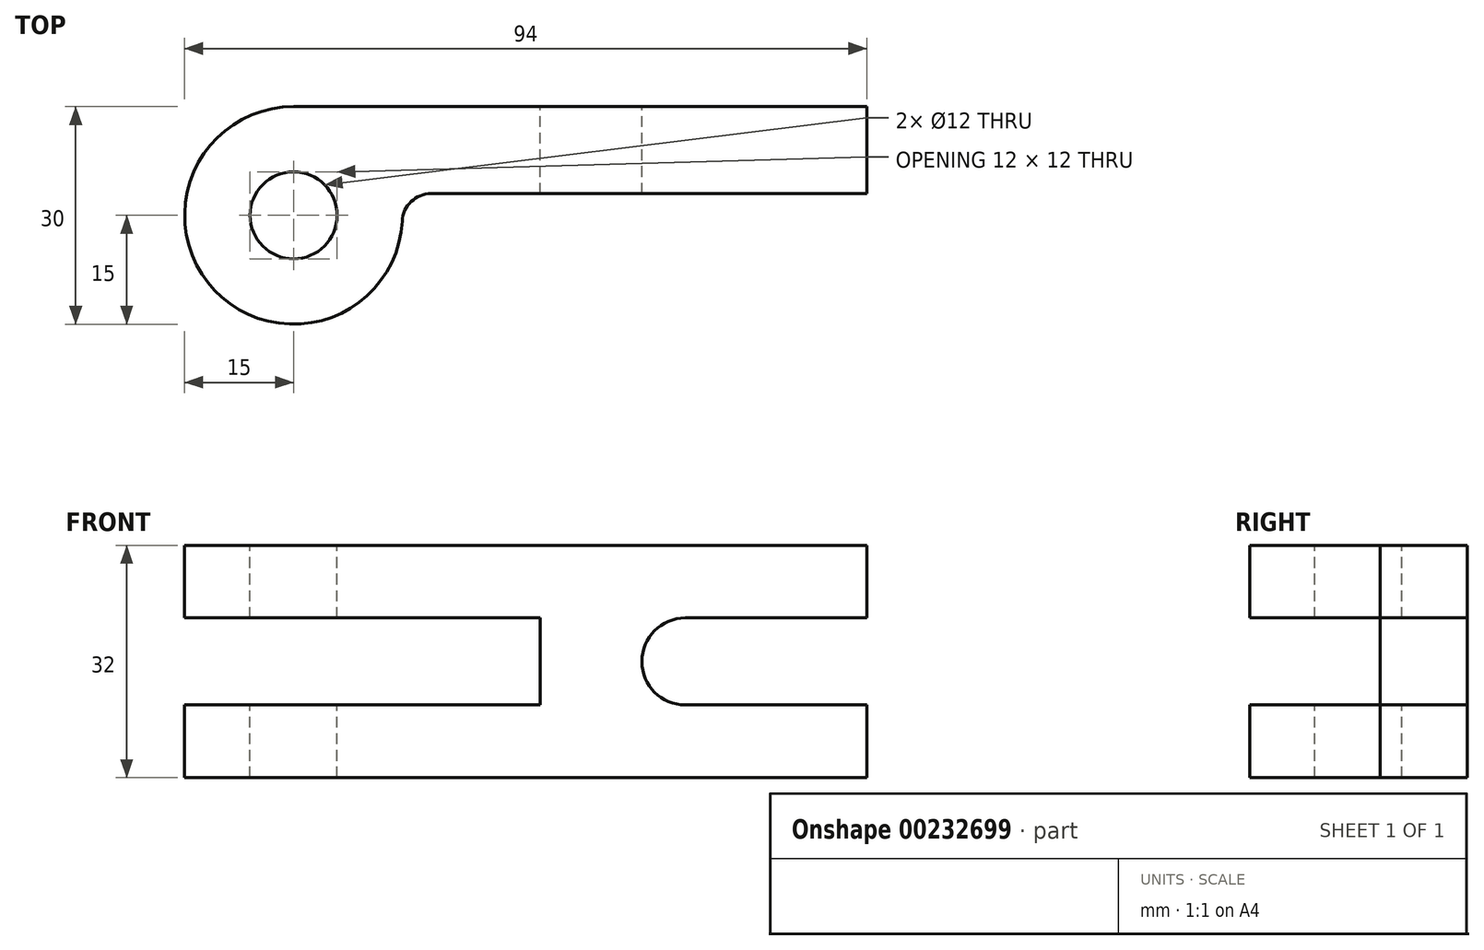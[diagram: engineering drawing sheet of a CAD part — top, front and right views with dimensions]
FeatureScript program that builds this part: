
annotation { "Feature Type Name" : "Feature", "Feature Type Description" : "" }
export const myFeature = defineFeature(function(context is Context, id is Id, definition is map)
    precondition{}
    {
        {
            var Q0;
            Q0=qCreatedBy(makeId("Front.planeOp"),FACE);
            var sketch = newSketch(context, id + "F0", { "sketchPlane" : qUnion([Q0])});
            skArc(sketch, "E0", {"start": v(0, -16) * mm, "mid": v(16, 0) * mm, "end": v(0, 16) * mm});
            skArc(sketch, "E1", {"start": v(0, -6) * mm, "mid": v(6, 0) * mm, "end": v(0, 6) * mm});
            skLineSegment(sketch, "E2", {"start": v(0, 16) * mm, "end": v(-94, 16) * mm});
            skLineSegment(sketch, "E3", {"start": v(-94, 16) * mm, "end": v(-94, 6) * mm});
            skLineSegment(sketch, "E4", {"start": v(-94, -16) * mm, "end": v(0, -16) * mm});
            skLineSegment(sketch, "E5", {"start": v(0, 6) * mm, "end": v(-25, 6) * mm});
            skLineSegment(sketch, "E6", {"start": v(0, -6) * mm, "end": v(-25, -6) * mm});
            skArc(sketch, "E7", {"start": v(-25, 6) * mm, "mid": v(-31, 0) * mm, "end": v(-25, -6) * mm});
            skLineSegment(sketch, "E8", {"start": v(-45, 6) * mm, "end": v(-45, -6) * mm});
            skLineSegment(sketch, "E9.trimOffspring", {"start": v(-94, -6) * mm, "end": v(-94, -16) * mm});
            skLineSegment(sketch, "E10.trimOffspring", {"start": v(-45, 6) * mm, "end": v(-94, 6) * mm});
            skLineSegment(sketch, "E11.trimOffspring", {"start": v(-45, -6) * mm, "end": v(-94, -6) * mm});
            skLineSegment(sketch, "E12", {"start": v(-45, 6) * mm, "end": v(-25, 6) * mm});
            skSolve(sketch);
        }
        {
            var Q0;
            Q0=makeQuery(id+"F0.imprint","IMPRINT",FACE,{"disambiguationData":[TD([[makeQuery(id+"F0.imprint","IMPRINT",EDGE,{"derivedFrom":sQuery(id+"F0.wireOp",EDGE,"E1")}),1.0]])]});
            var Q1;
            Q1=makeQuery(id+"F0.imprint","IMPRINT",FACE,{"disambiguationData":[TD([[makeQuery(id+"F0.imprint","IMPRINT",EDGE,{"derivedFrom":sQuery(id+"F0.wireOp",EDGE,"E0")}),1.0]])]});
            extrude(context, id + "F1", {"entities" : qUnion([Q0, Q1]), "depth" : 12 * mm});
        }
        {
            var Q0;
            Q0=makeQuery(id+"F0.imprint","IMPRINT",FACE,{"disambiguationData":[TD([[makeQuery(id+"F0.imprint","IMPRINT",EDGE,{"derivedFrom":sQuery(id+"F0.wireOp",EDGE,"E0")}),1.0]])]});
            extrude(context, id + "F2", {"entities" : qUnion([Q0]), "operationType" : NewBodyOperationType.ADD, "depth" : 30 * mm});
        }
        {
            var Q0;
            Q0=makeQuery(id+"F0.imprint","IMPRINT",FACE,{"disambiguationData":[TD([[makeQuery(id+"F0.imprint","IMPRINT",EDGE,{"derivedFrom":sQuery(id+"F0.wireOp",EDGE,"E1")}),1.0]])]});
            extrude(context, id + "F3", {"entities" : qUnion([Q0]), "operationType" : NewBodyOperationType.ADD, "depth" : 25 * mm});
        }
        {
            var Q0;
            Q0=makeQuery(id+"F0.imprint","IMPRINT",FACE,{"disambiguationData":[TD([[makeQuery(id+"F0.imprint","IMPRINT",EDGE,{"derivedFrom":sQuery(id+"F0.wireOp",EDGE,"E1")}),1.0]])]});
            extrude(context, id + "F4", {"entities" : qUnion([Q0]), "operationType" : NewBodyOperationType.REMOVE, "depth" : 25 * mm});
        }
        {
            var Q0;
            {var subQ0=sQuery(id+"F0.wireOp",EDGE,"E2");Q0=makeQuery(id+"F2.boolean.opBoolean","MERGE",FACE,{"derivedFrom":[makeQuery(id+"F1.opExtrude","SWEPT_FACE",FACE,{"disambiguationData":[OSD([subQ0])]}),makeQuery(id+"F2.opExtrude","SWEPT_FACE",FACE,{"disambiguationData":[OSD([subQ0])]})]});}
            var sketch = newSketch(context, id + "F5", { "sketchPlane" : qUnion([Q0])});
            skArc(sketch, "E13", {"start": v(-79, 0) * mm, "mid": v(-89.88, -25.32) * mm, "end": v(-64.02, -15.79) * mm});
            skCircle(sketch, "E14", {"center": v(-79, -15) * mm, "radius": 6 * mm});
            skLineSegment(sketch, "E15", {"start": v(-60.03, -12) * mm, "end": v(0, -12) * mm});
            skLineSegment(sketch, "E16.0.0", {"start": v(0, 0) * mm, "end": v(-94, 0) * mm});
            skLineSegment(sketch, "E16.0.1", {"start": v(-94, 0) * mm, "end": v(-94, -30) * mm});
            skLineSegment(sketch, "E16.0.2", {"start": v(-94, -30) * mm, "end": v(0, -30) * mm});
            skLineSegment(sketch, "E16.0.3", {"start": v(0, -30) * mm, "end": v(0, 0) * mm});
            skPoint(sketch, "E17.visualSharp", {"position": v(-64.3, -12) * mm});
            skArc(sketch, "E17.filletArc", {"start": v(-60.03, -12) * mm, "mid": v(-62.78, -13.1) * mm, "end": v(-64.02, -15.79) * mm});
            skLineSegment(sketch, "E18", {"start": v(16, 0) * mm, "end": v(16, -30) * mm});
            skLineSegment(sketch, "E19.bottom", {"start": v(0, 0) * mm, "end": v(33.35, 0) * mm});
            skLineSegment(sketch, "E19.top", {"start": v(0, -12) * mm, "end": v(33.35, -12) * mm});
            skLineSegment(sketch, "E19.left", {"start": v(0, 0) * mm, "end": v(0, -12) * mm});
            skLineSegment(sketch, "E19.right", {"start": v(33.35, 0) * mm, "end": v(33.35, -12) * mm});
            skSolve(sketch);
        }
        {
            var Q0;
            Q0=makeQuery(id+"F5.imprint","IMPRINT",FACE,{"disambiguationData":[TD([[makeQuery(id+"F5.imprint","IMPRINT",EDGE,{"derivedFrom":sQuery(id+"F5.wireOp",EDGE,"E14")}),-1.0]])]});
            var Q1;
            {var subQ5=sQuery(id+"F5.wireOp",EDGE,"E19.left");Q1=makeQuery(id+"F5.imprint","IMPRINT",FACE,{"disambiguationData":[TD([[makeQuery(id+"F5.imprint","IMPRINT",EDGE,{"derivedFrom":subQ5}),-1.0]])]});}
            extrude(context, id + "F6", {"entities" : qUnion([Q0, Q1]), "operationType" : NewBodyOperationType.INTERSECT, "oppositeDirection" : true, "depth" : 46.7 * mm});
        }
    });
